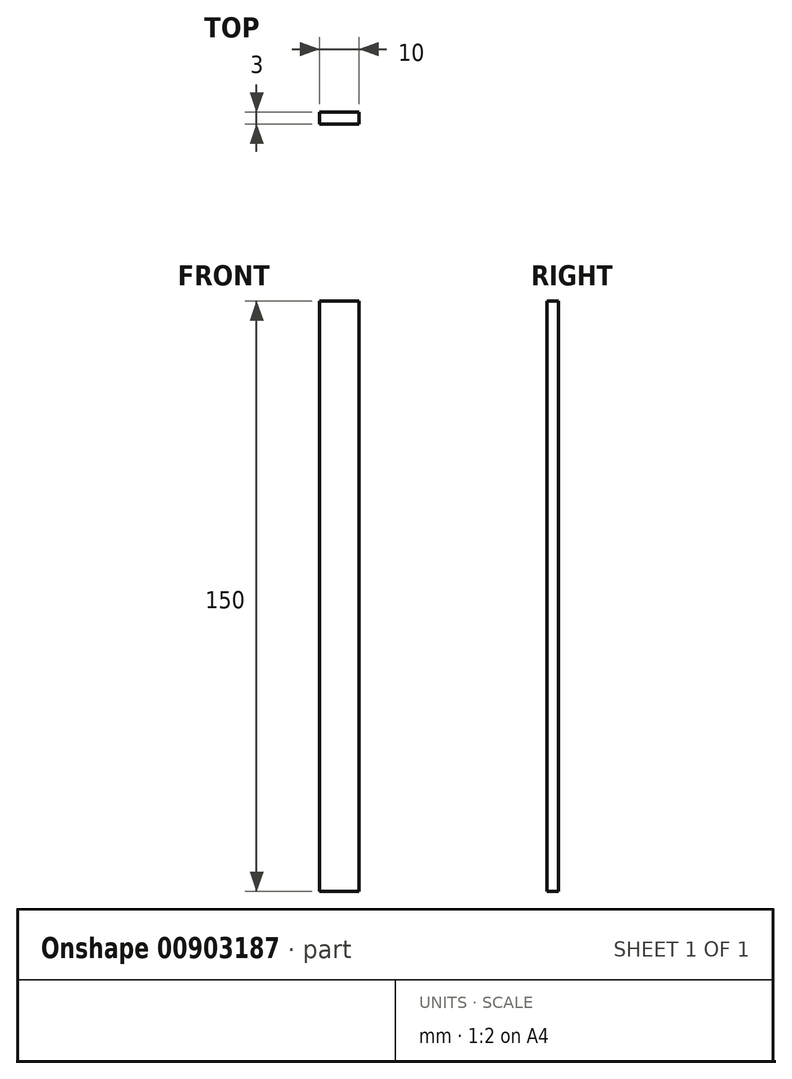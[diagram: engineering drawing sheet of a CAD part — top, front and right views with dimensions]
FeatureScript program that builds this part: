
annotation { "Feature Type Name" : "Feature", "Feature Type Description" : "" }
export const myFeature = defineFeature(function(context is Context, id is Id, definition is map)
    precondition{}
    {
        {
            var Q0;
            Q0=qCreatedBy(makeId("Front.planeOp"),FACE);
            var sketch = newSketch(context, id + "F0", { "sketchPlane" : qUnion([Q0])});
            skLineSegment(sketch, "E0.bottom", {"start": v(0, 0) * mm, "end": v(10, 0) * mm});
            skLineSegment(sketch, "E0.top", {"start": v(0, -150) * mm, "end": v(10, -150) * mm});
            skLineSegment(sketch, "E0.left", {"start": v(0, 0) * mm, "end": v(0, -150) * mm});
            skLineSegment(sketch, "E0.right", {"start": v(10, 0) * mm, "end": v(10, -150) * mm});
            skSolve(sketch);
        }
        {
            var Q0;
            Q0=makeQuery(id+"F0.imprint","IMPRINT",FACE,{"disambiguationData":[TD([[makeQuery(id+"F0.imprint","IMPRINT",EDGE,{"derivedFrom":sQuery(id+"F0.wireOp",EDGE,"E0.bottom")}),-1.0]])]});
            extrude(context, id + "F1", {"entities" : qUnion([Q0]), "depth" : 3 * mm, "offsetDistance" : 25 * mm});
        }
    });
